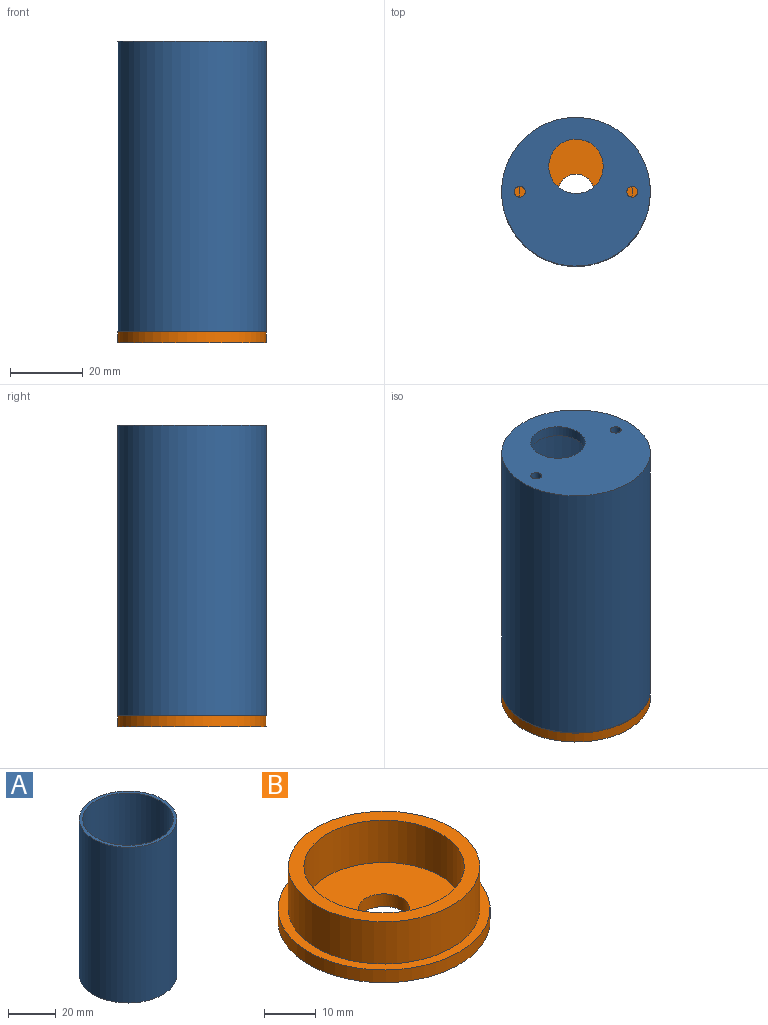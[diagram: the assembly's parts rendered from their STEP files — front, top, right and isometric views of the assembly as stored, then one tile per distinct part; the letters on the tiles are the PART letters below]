
ASSEMBLY  parts=2 mates=1
PART A: 8 faces, bbox 41x41x80 mm
  f0: cylinder r=19mm len=77mm, axis (0,0,-1), area 9192.3mm2, adj f2,f6
  f1: cylinder r=20.5mm len=80mm, axis (0,0,-1), area 10304.4mm2, adj f2,f3
  f2: plane 41x41mm, normal (0,0,1), area 186.1mm2, adj f0,f1
  f3: plane 41x41mm, normal (0,0,-1), area 1129.4mm2, adj f1,f4,f5,f7
  f4: cylinder r=1.5mm len=3mm, axis (0,0,-1), area 28.3mm2, adj f3,f6
  f5: cylinder r=1.5mm len=3mm, axis (0,0,-1), area 28.3mm2, adj f3,f6
  f6: plane 38x38mm, normal (0,0,1), area 943.3mm2, adj f0,f4,f5,f7
  f7: cylinder r=7.5mm len=15mm, axis (0,0,-1), area 141.4mm2, adj f3,f6
PART B: 8 faces, bbox 41x41x13 mm
  f0: cylinder r=20.5mm len=41mm, axis (0,0,-1), area 386.4mm2, adj f1,f2
  f1: plane 41x41mm, normal (0,0,1), area 245mm2, adj f0,f4
  f2: plane 41x41mm, normal (0,0,-1), area 1241.7mm2, adj f0,f7
  f3: cylinder r=15.5mm len=31mm, axis (0,0,-1), area 973.9mm2, adj f5,f6
  f4: cylinder r=18.5mm len=37mm, axis (0,0,-1), area 1162.4mm2, adj f1,f5
  f5: plane 37x37mm, normal (0,0,1), area 320.4mm2, adj f3,f4
  f6: plane 31x31mm, normal (0,0,1), area 676.2mm2, adj f3,f7
  f7: cylinder r=5mm len=10mm, axis (0,0,-1), area 94.2mm2, adj f2,f6
PLACE A rot(axis=(1,0,0),180deg) t=(12.5,2.19,142.6)mm
PLACE B rot(axis=(0,0,1),90deg) t=(12.5,2.19,59.5)mm
MATE fastened A.f0 <-> B.f3  axis (0,0,1) through (12.5,2.19,62.6)mm
